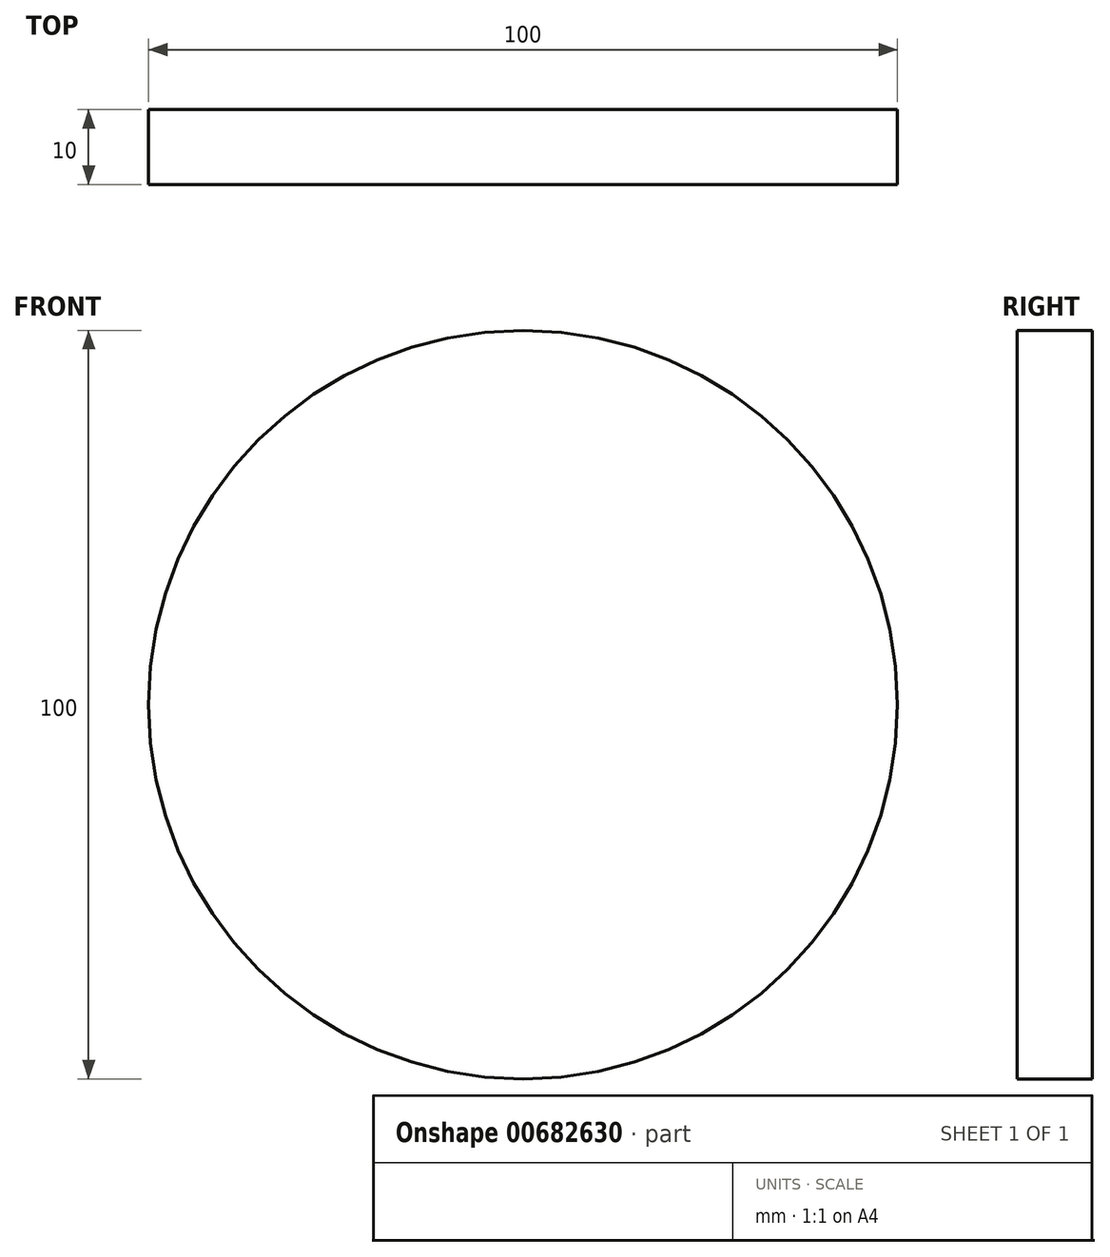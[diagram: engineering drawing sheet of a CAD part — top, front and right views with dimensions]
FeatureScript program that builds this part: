
annotation { "Feature Type Name" : "Feature", "Feature Type Description" : "" }
export const myFeature = defineFeature(function(context is Context, id is Id, definition is map)
    precondition{}
    {
        {
            var Q0;
            Q0=qCreatedBy(makeId("Front.planeOp"),FACE);
            var sketch = newSketch(context, id + "F0", { "sketchPlane" : qUnion([Q0])});
            skCircle(sketch, "E0", {"center": v(0, 0) * mm, "radius": 50 * mm});
            skSolve(sketch);
        }
        {
            var Q0;
            Q0=makeQuery(id+"F0.imprint","IMPRINT",FACE,{"disambiguationData":[TD([[makeQuery(id+"F0.imprint","IMPRINT",EDGE,{"derivedFrom":sQuery(id+"F0.wireOp",EDGE,"E0")}),1.0]])]});
            extrude(context, id + "F1", {"entities" : qUnion([Q0]), "depth" : 10 * mm, "offsetDistance" : 25 * mm});
        }
    });
